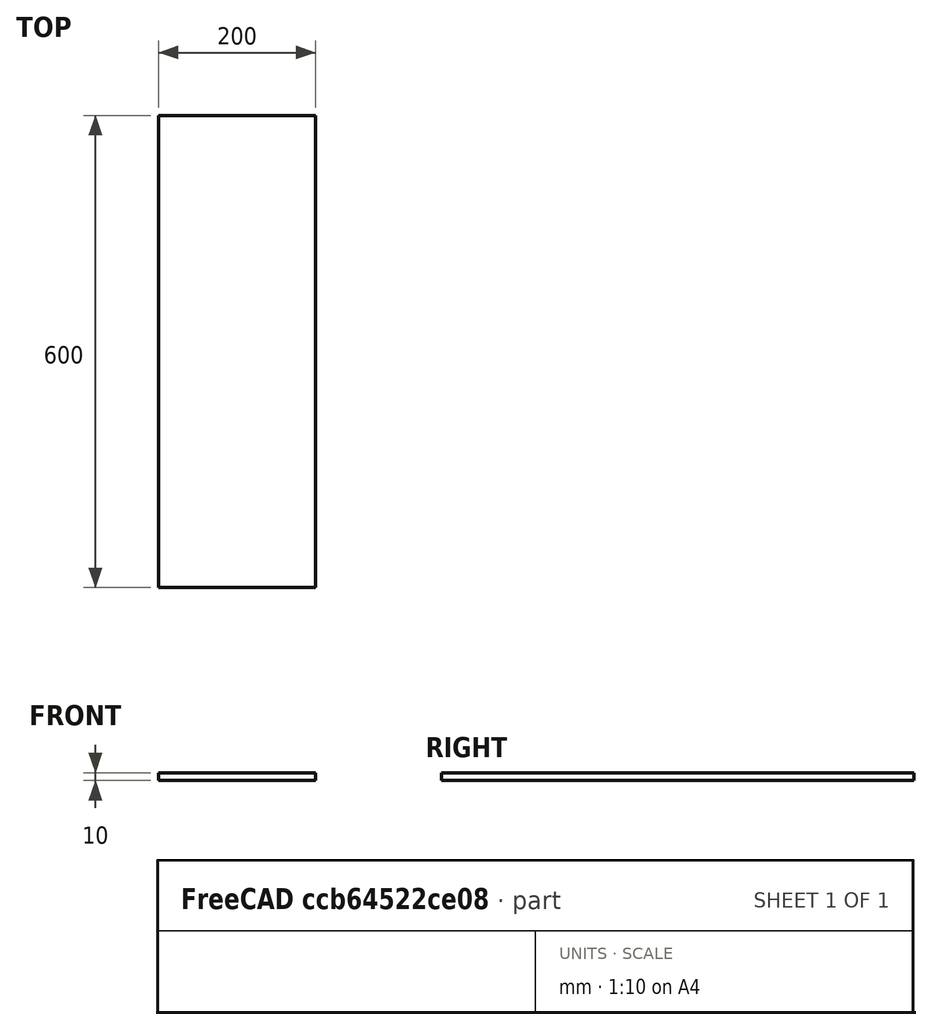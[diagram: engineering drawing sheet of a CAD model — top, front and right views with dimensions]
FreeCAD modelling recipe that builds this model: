
FCSTD DOCUMENT  (FreeCAD 0.19R24276 (Git))
Label: Osnovanie_2
License: All rights reserved
LicenseURL: http://en.wikipedia.org/wiki/All_rights_reserved
objects: Sketcher::SketchObject×1, PartDesign::Pad×1, PartDesign::Body×1
note: 4 computed .brp shape members not serialized (recipe doc carries the construction recipe); baked Part::Feature solids carry a one-line shape summary decoded from their .brp

FEATURE [Sketcher::SketchObject] Sketch
  FullyConstrained = true
  MapMode = 5
  Support = -> [XY_Plane]
  sketch-geometry (4):
    g0: LineSegment StartX=0 StartY=0 StartZ=0 EndX=200 EndY=0 EndZ=0
    g1: LineSegment StartX=200 StartY=0 StartZ=0 EndX=200 EndY=600 EndZ=0
    g2: LineSegment StartX=200 StartY=600 StartZ=0 EndX=0 EndY=600 EndZ=0
    g3: LineSegment StartX=0 StartY=600 StartZ=0 EndX=0 EndY=0 EndZ=0
  constraints (11):
    c: Coincident(g0,g1)
    c: Coincident(g1,g2)
    c: Coincident(g2,g3)
    c: Coincident(g3,g0)
    c: Horizontal(g0)
    c: Horizontal(g2)
    c: Vertical(g1)
    c: Vertical(g3)
    c: Coincident(g0,g-1)
    c: Distance(g0) = 200
    c: Distance(g1) = 600
FEATURE [PartDesign::Pad] Pad
  Direction = (1,1,1)
  Length = 10
  Length2 = 100
  Profile = -> Sketch
  Type = 0
FEATURE [PartDesign::Body] Body
  Group = -> [Sketch,Pad]
  Origin = -> Origin
  Tip = -> Pad
